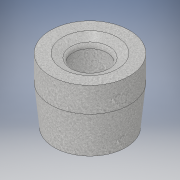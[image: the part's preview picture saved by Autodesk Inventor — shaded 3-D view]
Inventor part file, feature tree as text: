
AUTODESK INVENTOR PART (.ipt)
format: ipt  version: 2017 SP1 (Build 210196100, 196)  size: 188,928 bytes
history: native  units: in
note: dims shown in document units (in); Inventor stores cm internally (conversion verified against a paired STEP export)
features: revolve x1, sketch x1
ambient origin geometry x8: Origin, YZ Plane, XZ Plane, XY Plane, X Axis, Y Axis, Z Axis, Center Point
bodies: Solid1 (feature_tree)
feature tree (2):
  revolve  "Revolution1"  [1 undecoded]
  sketch  "Sketch1"  dims[d0=1.13in d1=3.75in d2=0.125in d3=0.1718in d5=1.0in d6=1.0in d7=90.0deg d8=0.5in d9=15.0deg d12=1.25in d13=0.25in d16=0.5in d17=0.5in d18=0.5in d19=2.5in d20=0.5in d22=0.375in d23=0.25in d25=0.234in d27=0.125in d28=0.25in d29=1.0in d30=4.25in d31=0.25in d33=0.8014in d34=15.0deg d35=0.125in d36=1.0in d37=90.0deg]
note: 1 required parameter value undecoded (feature->parameter linkage not recoverable at this tier; creation-order binding heuristic only, values carry confidence <= 0.55)
